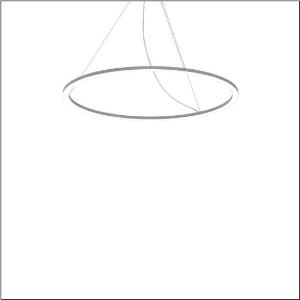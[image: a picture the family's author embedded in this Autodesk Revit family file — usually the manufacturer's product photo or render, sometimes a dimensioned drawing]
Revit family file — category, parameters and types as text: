
# Revit family: silica_r__21_ring-d_5pjbd3d1204a_4b66
name_source: partatom
category: Lighting Fixtures
units: mm (PartAtom-declared; Revit-internal decimal feet)

## family parameters
Cut with Voids When Loaded = No
Host = Face
Light Source = No
Part Type = Normal
Room Calculation Point = No
Round Connector Dimension = Use Diameter
Shared = No

## types (1)
- Silica® 21 Ring-D (1 x LED, 8050 lm, 94 W, 3000K)
    Apparent Load = 94 VA
    CIE Flux Codes = 37 69 92 100 100
    Color Rendering = 80
    Color Temperature = 3000K
    Default Elevation = 1800 mm
    Description = Silica® 21 Ring-D, suspended luminaire, of PMMA, frosted, light emission: ring underside luminous distribution, primary light characteristic: symmetric, installation type: suspended mounting, LED, rated luminous flux: 8.050lm, luminous efficacy: 86lm/W, light colour: 830, colour temperature: 3000K, control gear: DALI 2, with terminal, 5-pole, mains connection: 230V, AC/DC, 0/50..60Hz, rated input power: 94W, housing, of extruded aluminium section, metallic grey (RAL 9006), diameter: 1.100mm, ceiling canopy, metallic grey (RAL 9006), protection rating (lamp compartment): IP40, insulation class (complete): insulation class I (protective earthing), certification: CE, impact resistance: IK02, permissible operating ambient temperature: 0..+35°C, packaging unit: 1 piece
    Height = 25 mm  [stored 0.082021 ft]
    Lamp = 1 x LED
    Lamp Light Flux = 8050 lm
    Lamp Power = 94 W
    Lamp count = 1
    Length = 1100 mm
    Luminous efficacy = 86 lm/W
    Manufacturer = Siteco
    ModVariant = No
    Model = 5PJBD3D1204A
    Mounting Place = Ceiling
    Mounting Type = Pendant
    Number of Poles = 1
    OnlyDefault = Yes
    Power Factor = 1
    Product Name = Silica® 21 Ring-D
    Product group = suspended luminaire
    ProductGroupID = 905
    Protection Class = Protection class I
    Protection Degree = IP 40
    RLX_Detail_Level = 1
    RLX_Emergency_Light_Flux = 0 lm
    RLX_Emergency_Type = 0
    RLX_Emergency_Type_DB = No
    RlxData = <blob elided: 14593 chars, md5=bf6fa577>
    Socket = socket
    Standby Power = 0 W
    System Light Flux = 8050 lm
    System Power = 94 W
    Type Comments = Product without accessories
    Type Image = l_1251746.jpg
    URL = http://relux.com
    VarID = ---
    Voltage = 0 V
    Weight = 0.00 kg
    Width = 0 mm  [stored 0 ft]

note: [stored X ft] marks values corroborated as IEEE doubles in the binary element streams (Revit-internal decimal feet)

## geometry (parser evidence)
native form markers: Sweep x12
no freeform markers — native parametric forms only
